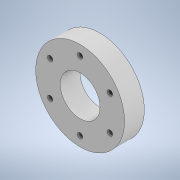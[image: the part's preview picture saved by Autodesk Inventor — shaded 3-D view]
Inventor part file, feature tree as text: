
AUTODESK INVENTOR PART (.ipt)
format: ipt  version: 2020 (Build 240168000, 168)  size: 119,808 bytes
history: native  units: in
note: dims shown in document units (in); Inventor stores cm internally (conversion verified against a paired STEP export)
features: extrude x1, sketch x1
ambient origin geometry x8: Origin, YZ Plane, XZ Plane, XY Plane, X Axis, Y Axis, Z Axis, Center Point
bodies: Solid1 (feature_tree)
feature tree (2):
  extrude  "Extrusion1"  Depth=1.75in
  sketch  "Sketch1"  dims[d0=2.0157in d1=1.75in d2=0.2656in d3=2.3622in d5=360.0deg d7=4.5in d8=1.0in d9=0.0in]
